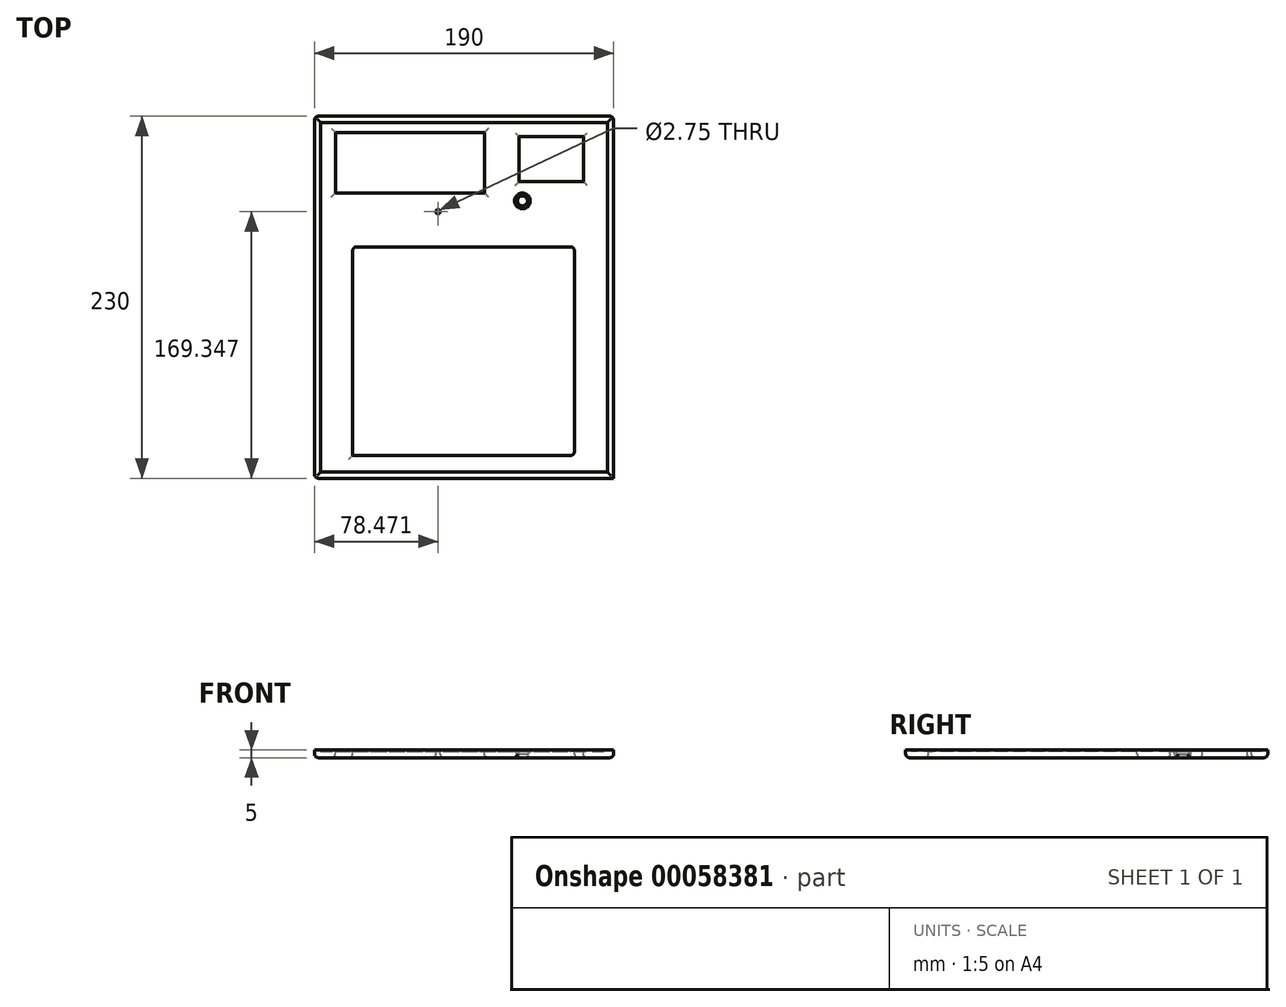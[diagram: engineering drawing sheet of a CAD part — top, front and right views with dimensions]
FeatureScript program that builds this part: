
annotation { "Feature Type Name" : "Feature", "Feature Type Description" : "" }
export const myFeature = defineFeature(function(context is Context, id is Id, definition is map)
    precondition{}
    {
        {
            var Q0;
            Q0=qCreatedBy(makeId("Top.planeOp"),FACE);
            var sketch = newSketch(context, id + "F0", { "sketchPlane" : qUnion([Q0])});
            skLineSegment(sketch, "E0.bottom", {"start": v(-100.1, 140.46) * mm, "end": v(89.9, 140.46) * mm});
            skLineSegment(sketch, "E0.top", {"start": v(-100.1, -89.54) * mm, "end": v(89.9, -89.54) * mm});
            skLineSegment(sketch, "E0.left", {"start": v(-100.1, 140.46) * mm, "end": v(-100.1, -89.54) * mm});
            skLineSegment(sketch, "E0.right", {"start": v(89.9, 140.46) * mm, "end": v(89.9, -89.54) * mm});
            skSolve(sketch);
        }
        {
            var Q0;
            Q0 = qSketchRegion(id + "F0", true);
            extrude(context, id + "F1", {"entities" : qUnion([Q0]), "depth" : 5 * mm});
        }
        {
            var Q0;
            Q0=makeQuery(id+"F1.opExtrude","CAP_FACE",FACE,{"disambiguationData":[OSD([sQuery(id+"F0.wireOp",EDGE,"E0.bottom"),sQuery(id+"F0.wireOp",EDGE,"E0.top"),sQuery(id+"F0.wireOp",EDGE,"E0.left"),sQuery(id+"F0.wireOp",EDGE,"E0.right")])],"isStart":false});
            shell(context, id + "F2", {"entities" : qUnion([Q0]), "thickness" : 4 * mm});
        }
        {
            var Q0;
            Q0=makeQuery(id+"F2.opShell","OFFSET_FACE",FACE,{"disambiguationData":[OSD([sQuery(id+"F0.wireOp",EDGE,"E0.bottom"),sQuery(id+"F0.wireOp",EDGE,"E0.top"),sQuery(id+"F0.wireOp",EDGE,"E0.left"),sQuery(id+"F0.wireOp",EDGE,"E0.right")])]});
            var sketch = newSketch(context, id + "F3", { "sketchPlane" : qUnion([Q0])});
            skPoint(sketch, "E1", {"position": v(-21.62, 79.8) * mm});
            skSolve(sketch);
        }
        {
            var Q0;
            Q0=sQuery(id+"F3.wireOp",VERTEX,"E1");
            var Q1;
            Q1=makeQuery(id+"F1.opExtrude","SWEPT_BODY",BODY,{"disambiguationData":[OSD([sQuery(id+"F0.wireOp",EDGE,"E0.bottom"),sQuery(id+"F0.wireOp",EDGE,"E0.top"),sQuery(id+"F0.wireOp",EDGE,"E0.left"),sQuery(id+"F0.wireOp",EDGE,"E0.right")])]});
            hole(context, id + "F4", {"style" : HoleStyle.SIMPLE, "holeDiameter" : 2.75 * mm, "endStyle" : HoleEndStyle.THROUGH, "locations" : qUnion([Q0]), "scope" : qUnion([Q1])});
        }
        {
            var Q0;
            Q0=makeQuery(id+"F2.opShell","OFFSET_FACE",FACE,{"disambiguationData":[OSD([sQuery(id+"F0.wireOp",EDGE,"E0.bottom"),sQuery(id+"F0.wireOp",EDGE,"E0.top"),sQuery(id+"F0.wireOp",EDGE,"E0.left"),sQuery(id+"F0.wireOp",EDGE,"E0.right")])]});
            var sketch = newSketch(context, id + "F5", { "sketchPlane" : qUnion([Q0])});
            skPoint(sketch, "E2", {"position": v(31.98, 86.66) * mm});
            skSolve(sketch);
        }
        {
            var Q0;
            Q0=sQuery(id+"F5.wireOp",VERTEX,"E2");
            var Q1;
            Q1=makeQuery(id+"F1.opExtrude","SWEPT_BODY",BODY,{"disambiguationData":[OSD([sQuery(id+"F0.wireOp",EDGE,"E0.bottom"),sQuery(id+"F0.wireOp",EDGE,"E0.top"),sQuery(id+"F0.wireOp",EDGE,"E0.left"),sQuery(id+"F0.wireOp",EDGE,"E0.right")])]});
            hole(context, id + "F6", {"style" : HoleStyle.C_SINK, "holeDiameter" : 6.35 * mm, "cSinkDiameter" : 10 * mm, "endStyle" : HoleEndStyle.THROUGH, "locations" : qUnion([Q0]), "scope" : qUnion([Q1]), "cSinkAngle" : 90 * degree});
        }
        {
            var Q0;
            Q0=makeQuery(id+"F2.opShell","OFFSET_FACE",FACE,{"disambiguationData":[OSD([sQuery(id+"F0.wireOp",EDGE,"E0.bottom"),sQuery(id+"F0.wireOp",EDGE,"E0.top"),sQuery(id+"F0.wireOp",EDGE,"E0.left"),sQuery(id+"F0.wireOp",EDGE,"E0.right")])]});
            var sketch = newSketch(context, id + "F7", { "sketchPlane" : qUnion([Q0])});
            skLineSegment(sketch, "E3.bottom", {"start": v(-75.81, 57.47) * mm, "end": v(65.04, 57.47) * mm});
            skLineSegment(sketch, "E3.top", {"start": v(-75.81, -75.04) * mm, "end": v(65.04, -75.04) * mm});
            skLineSegment(sketch, "E3.left", {"start": v(-75.81, 57.47) * mm, "end": v(-75.81, -75.04) * mm});
            skLineSegment(sketch, "E3.right", {"start": v(65.04, 57.47) * mm, "end": v(65.04, -75.04) * mm});
            skLineSegment(sketch, "E4.bottom", {"start": v(-86.83, 130.13) * mm, "end": v(7.86, 130.13) * mm});
            skLineSegment(sketch, "E4.top", {"start": v(-86.83, 91.72) * mm, "end": v(7.86, 91.72) * mm});
            skLineSegment(sketch, "E4.left", {"start": v(-86.83, 130.13) * mm, "end": v(-86.83, 91.72) * mm});
            skLineSegment(sketch, "E4.right", {"start": v(7.86, 130.13) * mm, "end": v(7.86, 91.72) * mm});
            skLineSegment(sketch, "E5.bottom", {"start": v(30, 127.37) * mm, "end": v(70.66, 127.37) * mm});
            skLineSegment(sketch, "E5.top", {"start": v(30, 99) * mm, "end": v(70.66, 99) * mm});
            skLineSegment(sketch, "E5.left", {"start": v(30, 127.37) * mm, "end": v(30, 99) * mm});
            skLineSegment(sketch, "E5.right", {"start": v(70.66, 127.37) * mm, "end": v(70.66, 99) * mm});
            skSolve(sketch);
        }
        {
            var Q0;
            Q0 = qSketchRegion(id + "F7", true);
            extrude(context, id + "F8", {"entities" : qUnion([Q0]), "operationType" : NewBodyOperationType.REMOVE, "oppositeDirection" : true, "depth" : 25 * mm});
        }
        {
            var Q0;
            Q0=makeQuery(id+"F1.opExtrude","CAP_FACE",FACE,{"disambiguationData":[OSD([sQuery(id+"F0.wireOp",EDGE,"E0.bottom"),sQuery(id+"F0.wireOp",EDGE,"E0.top"),sQuery(id+"F0.wireOp",EDGE,"E0.left"),sQuery(id+"F0.wireOp",EDGE,"E0.right")])],"isStart":true});
            var Q1;
            Q1=makeQuery(id+"F1.opExtrude","SWEPT_EDGE",EDGE,{"disambiguationData":[OSD([sQuery(id+"F0.wireOp",EDGE,"E0.top"),sQuery(id+"F0.wireOp",EDGE,"E0.left")])]});
            var Q2;
            Q2=makeQuery(id+"F1.opExtrude","SWEPT_EDGE",EDGE,{"disambiguationData":[OSD([sQuery(id+"F0.wireOp",EDGE,"E0.bottom"),sQuery(id+"F0.wireOp",EDGE,"E0.right")])]});
            var Q3;
            Q3=makeQuery(id+"F1.opExtrude","SWEPT_EDGE",EDGE,{"disambiguationData":[OSD([sQuery(id+"F0.wireOp",EDGE,"E0.bottom"),sQuery(id+"F0.wireOp",EDGE,"E0.left")])]});
            var Q4;
            {var subQ0=sQuery(id+"F0.wireOp",EDGE,"E0.bottom");Q4=makeQuery(id+"F2.opShell","OFFSET_EDGE",EDGE,{"disambiguationData":[OSD([subQ0]),TDD([makeQuery(id+"F1.opExtrude","CAP_EDGE",EDGE,{"disambiguationData":[OSD([subQ0])],"isStart":false})])]});}
            var Q5;
            {var subQ0=sQuery(id+"F0.wireOp",EDGE,"E0.left");Q5=makeQuery(id+"F2.opShell","OFFSET_EDGE",EDGE,{"disambiguationData":[OSD([subQ0]),TDD([makeQuery(id+"F1.opExtrude","CAP_EDGE",EDGE,{"disambiguationData":[OSD([subQ0])],"isStart":false})])]});}
            var Q6;
            {var subQ0=sQuery(id+"F0.wireOp",EDGE,"E0.right");Q6=makeQuery(id+"F2.opShell","OFFSET_EDGE",EDGE,{"disambiguationData":[OSD([subQ0]),TDD([makeQuery(id+"F1.opExtrude","CAP_EDGE",EDGE,{"disambiguationData":[OSD([subQ0])],"isStart":false})])]});}
            var Q7;
            {var subQ0=sQuery(id+"F0.wireOp",EDGE,"E0.top");Q7=makeQuery(id+"F2.opShell","OFFSET_EDGE",EDGE,{"disambiguationData":[OSD([subQ0]),TDD([makeQuery(id+"F1.opExtrude","CAP_EDGE",EDGE,{"disambiguationData":[OSD([subQ0])],"isStart":false})])]});}
            var Q8;
            Q8=makeQuery(id+"F8.boolean.opBoolean","COPY",EDGE,{"derivedFrom":makeQuery(id+"F8.opExtrude","SWEPT_EDGE",EDGE,{"disambiguationData":[OSD([sQuery(id+"F7.wireOp",EDGE,"E3.bottom"),sQuery(id+"F7.wireOp",EDGE,"E3.left")])]})});
            var Q9;
            Q9=makeQuery(id+"F8.boolean.opBoolean","COPY",EDGE,{"derivedFrom":makeQuery(id+"F8.opExtrude","SWEPT_EDGE",EDGE,{"disambiguationData":[OSD([sQuery(id+"F7.wireOp",EDGE,"E3.bottom"),sQuery(id+"F7.wireOp",EDGE,"E3.right")])]})});
            var Q10;
            Q10=makeQuery(id+"F8.boolean.opBoolean","COPY",EDGE,{"derivedFrom":makeQuery(id+"F8.opExtrude","SWEPT_EDGE",EDGE,{"disambiguationData":[OSD([sQuery(id+"F7.wireOp",EDGE,"E3.top"),sQuery(id+"F7.wireOp",EDGE,"E3.right")])]})});
            fillet(context, id + "F9", {"entities" : qUnion([Q0, Q1, Q2, Q3, Q4, Q5, Q6, Q7, Q8, Q9, Q10]), "radius" : 2.5 * mm, "tangentPropagation" : true, "allowEdgeOverflow" : false});
        }
    });
